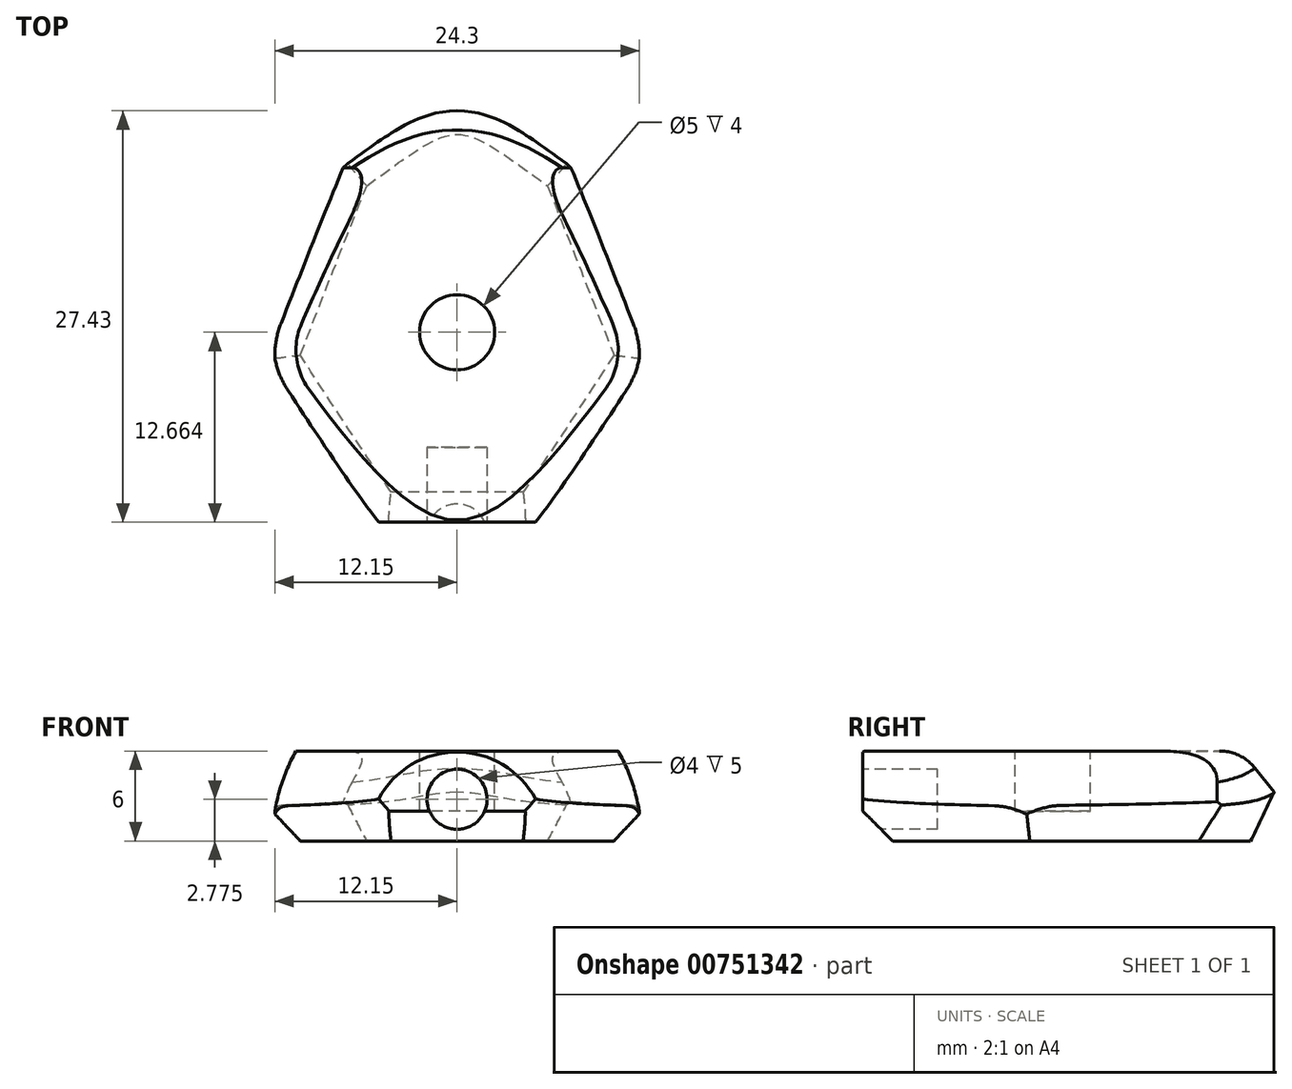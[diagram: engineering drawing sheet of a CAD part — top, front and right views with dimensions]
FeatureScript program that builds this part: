
annotation { "Feature Type Name" : "Feature", "Feature Type Description" : "" }
export const myFeature = defineFeature(function(context is Context, id is Id, definition is map)
    precondition{}
    {
        {
            var Q0;
            Q0=qCreatedBy(makeId("Top.planeOp"),FACE);
            var sketch = newSketch(context, id + "F0", { "sketchPlane" : qUnion([Q0])});
            skLineSegment(sketch, "E0", {"start": v(0, 24.22) * mm, "end": v(8.02, 17.86) * mm});
            skLineSegment(sketch, "E1", {"start": v(8.02, 17.86) * mm, "end": v(12.87, 5.13) * mm});
            skLineSegment(sketch, "E2", {"start": v(12.87, 5.13) * mm, "end": v(5.93, -5.78) * mm});
            skLineSegment(sketch, "E3", {"start": v(5.93, -5.78) * mm, "end": v(0, -5.78) * mm});
            skLineSegment(sketch, "E4", {"start": v(0, 24.22) * mm, "end": v(0, -5.78) * mm});
            skSolve(sketch);
        }
        {
            var Q0;
            Q0=makeQuery(id+"F0.imprint","IMPRINT",FACE,{"disambiguationData":[TD([[makeQuery(id+"F0.imprint","IMPRINT",EDGE,{"derivedFrom":sQuery(id+"F0.wireOp",EDGE,"E0")}),-1.0]])]});
            var Q1;
            Q1=sQuery(id+"F0.wireOp",EDGE,"E4");
            revolve(context, id + "F1", {"surfaceOperationType" : NewSurfaceOperationType.NEW, "entities" : qUnion([Q0]), "axis" : qUnion([Q1]), "revolveType" : RevolveType.ONE_DIRECTION, "angle" : 180 * degree});
        }
        {
            var Q0;
            Q0=qCreatedBy(makeId("Top.planeOp"),FACE);
            cPlane(context, id + "F2", {"entities" : qUnion([Q0]), "cplaneType" : CPlaneType.OFFSET, "offset" : 25 * mm, "width" : 150 * mm, "height" : 150 * mm});
        }
        {
            var Q0;
            Q0=qCreatedBy(id+"F2.planeOp",FACE);
            var sketch = newSketch(context, id + "F3", { "sketchPlane" : qUnion([Q0])});
            skLineSegment(sketch, "E5.bottom", {"start": v(27.95, -14.4) * mm, "end": v(-30.05, -14.4) * mm});
            skLineSegment(sketch, "E5.top", {"start": v(27.95, 47.24) * mm, "end": v(-30.05, 47.24) * mm});
            skLineSegment(sketch, "E5.left", {"start": v(27.95, -14.4) * mm, "end": v(27.95, 47.24) * mm});
            skLineSegment(sketch, "E5.right", {"start": v(-30.05, -14.4) * mm, "end": v(-30.05, 47.24) * mm});
            skSolve(sketch);
        }
        {
            var Q0;
            Q0=makeQuery(id+"F3.imprint","IMPRINT",FACE,{"disambiguationData":[TD([[makeQuery(id+"F3.imprint","IMPRINT",EDGE,{"derivedFrom":sQuery(id+"F3.wireOp",EDGE,"E5.bottom")}),-1.0]])]});
            extrude(context, id + "F4", {"entities" : qUnion([Q0]), "operationType" : NewBodyOperationType.REMOVE, "oppositeDirection" : true, "depth" : 19 * mm, "offsetDistance" : 25 * mm});
        }
        {
            var Q0;
            Q0=makeQuery(id+"F1.opRevolve","CAP_EDGE",EDGE,{"disambiguationData":[OSD([sQuery(id+"F0.wireOp",EDGE,"E1")])],"isStart":false});
            var Q1;
            Q1=makeQuery(id+"F1.opRevolve","CAP_EDGE",EDGE,{"disambiguationData":[OSD([sQuery(id+"F0.wireOp",EDGE,"E0")])],"isStart":false});
            var Q2;
            Q2=makeQuery(id+"F1.opRevolve","CAP_EDGE",EDGE,{"disambiguationData":[OSD([sQuery(id+"F0.wireOp",EDGE,"E2")])],"isStart":false});
            var Q3;
            Q3=makeQuery(id+"F1.opRevolve","CAP_EDGE",EDGE,{"disambiguationData":[OSD([sQuery(id+"F0.wireOp",EDGE,"E1")])],"isStart":true});
            var Q4;
            Q4=makeQuery(id+"F1.opRevolve","CAP_EDGE",EDGE,{"disambiguationData":[OSD([sQuery(id+"F0.wireOp",EDGE,"E2")])],"isStart":true});
            var Q5;
            Q5=makeQuery(id+"F1.opRevolve","CAP_EDGE",EDGE,{"disambiguationData":[OSD([sQuery(id+"F0.wireOp",EDGE,"E3")])],"isStart":true});
            chamfer(context, id + "F5", {"entities" : qUnion([Q0, Q1, Q2, Q3, Q4, Q5]), "width" : 2 * mm, "tangentPropagation" : true});
        }
        {
            var Q0;
            Q0=makeQuery(id+"F4.boolean.opBoolean","INTERSECT",EDGE,{"derivedFrom":[makeQuery(id+"F1.opRevolve","SWEPT_FACE",FACE,{"disambiguationData":[OSD([sQuery(id+"F0.wireOp",EDGE,"E0")])]}),makeQuery(id+"F4.opExtrude","CAP_FACE",FACE,{"disambiguationData":[OSD([sQuery(id+"F3.wireOp",EDGE,"E5.bottom"),sQuery(id+"F3.wireOp",EDGE,"E5.top"),sQuery(id+"F3.wireOp",EDGE,"E5.left"),sQuery(id+"F3.wireOp",EDGE,"E5.right")])],"isStart":false})]});
            fillet(context, id + "F6", {"entities" : qUnion([Q0]), "radius" : 3 * mm, "tangentPropagation" : true, "allowEdgeOverflow" : false});
        }
        {
            var Q0;
            Q0=makeQuery(id+"F4.boolean.opBoolean","SPLIT",EDGE,{"disambiguationData":[OD(0.0)],"derivedFrom":makeQuery(id+"F1.opRevolve","SWEPT_EDGE",EDGE,{"disambiguationData":[OSD([sQuery(id+"F0.wireOp",EDGE,"E1"),sQuery(id+"F0.wireOp",EDGE,"E2")])]})});
            var Q1;
            Q1=makeQuery(id+"F4.boolean.opBoolean","SPLIT",EDGE,{"disambiguationData":[OD(1.0)],"derivedFrom":makeQuery(id+"F1.opRevolve","SWEPT_EDGE",EDGE,{"disambiguationData":[OSD([sQuery(id+"F0.wireOp",EDGE,"E1"),sQuery(id+"F0.wireOp",EDGE,"E2")])]})});
            fillet(context, id + "F7", {"entities" : qUnion([Q0, Q1]), "radius" : 5 * mm, "tangentPropagation" : true, "allowEdgeOverflow" : false});
        }
        {
            var Q0;
            Q0=makeQuery(id+"F1.opRevolve","SWEPT_FACE",FACE,{"disambiguationData":[OSD([sQuery(id+"F0.wireOp",EDGE,"E3")])]});
            var sketch = newSketch(context, id + "F8", { "sketchPlane" : qUnion([Q0])});
            skCircle(sketch, "E6", {"center": v(0, 2.77) * mm, "radius": 2 * mm});
            skSolve(sketch);
        }
        {
            var Q0;
            Q0 = qSketchRegion(id + "F8", true);
            extrude(context, id + "F9", {"entities" : qUnion([Q0]), "operationType" : NewBodyOperationType.REMOVE, "oppositeDirection" : true, "depth" : 5 * mm, "offsetDistance" : 25 * mm});
        }
        {
            var Q0;
            Q0=makeQuery(id+"F4.boolean.opBoolean","COPY",FACE,{"derivedFrom":makeQuery(id+"F4.opExtrude","CAP_FACE",FACE,{"disambiguationData":[OSD([sQuery(id+"F3.wireOp",EDGE,"E5.bottom"),sQuery(id+"F3.wireOp",EDGE,"E5.top"),sQuery(id+"F3.wireOp",EDGE,"E5.left"),sQuery(id+"F3.wireOp",EDGE,"E5.right")])],"isStart":false})});
            var sketch = newSketch(context, id + "F10", { "sketchPlane" : qUnion([Q0])});
            skCircle(sketch, "E7", {"center": v(0, 6.88) * mm, "radius": 2.5 * mm});
            skSolve(sketch);
        }
        {
            var Q0;
            Q0=makeQuery(id+"F10.imprint","IMPRINT",FACE,{"disambiguationData":[TD([[makeQuery(id+"F10.imprint","IMPRINT",EDGE,{"derivedFrom":sQuery(id+"F10.wireOp",EDGE,"E7")}),1.0]])]});
            extrude(context, id + "F11", {"entities" : qUnion([Q0]), "operationType" : NewBodyOperationType.REMOVE, "oppositeDirection" : true, "depth" : 4 * mm, "offsetDistance" : 25 * mm});
        }
    });
